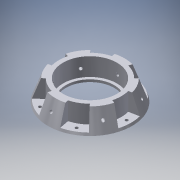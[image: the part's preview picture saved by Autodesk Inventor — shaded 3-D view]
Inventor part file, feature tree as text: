
AUTODESK INVENTOR PART (.ipt)
format: ipt  version: 2017 (Build 210142000, 142)  size: 261,120 bytes
history: native  units: in
note: dims shown in document units (in); Inventor stores cm internally (conversion verified against a paired STEP export)
features: sketch x6, extrude x3, hole x2, pattern_circular x2, plane x1, draft x1, projected_geometry x1
ambient origin geometry x8: Origin, YZ Plane, XZ Plane, XY Plane, X Axis, Y Axis, Z Axis, Center Point
bodies: Solid1 (feature_tree)
feature tree (16):
  extrude  "Extrusion1"  Depth=7.0in
  extrude  "Extrusion4"  Depth=5.21in
  hole  "Hole4"  [1 undecoded]
  pattern_circular  "Circular Pattern4"  Count=6 Angle=360.0deg
  extrude  "Extrusion5"  TaperAngle=30.0deg  [1 undecoded]
  plane  "Work Plane4"
  hole  "Hole5"  [1 undecoded]
  pattern_circular  "Circular Pattern5"  [2 undecoded]
  sketch  "Sketch13"  dims[d55=0.25in d56=0.75in d57=0.375in d58=0.25in d59=0.5635in d60=1.0in d61=0.8108in d62=2.3622in d63=360.0deg d71=30.0deg d72=1.5in d73=0.0in d74=0.85in d75=0.25in d76=0.25in d77=0.75in d78=0.375in d79=0.25in d80=0.5635in d81=2.0in d82=0.0in d83=2.3622in d84=360.0deg d86=0.1374in d12=1.0in d13=1.0in]
  draft  "FaceDraft1"
  sketch  "Sketch1"  dims[d0=4.026in d1=7.0in]
  sketch  "Sketch2"  dims[d2=0.2in d3=0.0in d4=5.21in]
  sketch  "Sketch9"  dims[d47=4.5in d48=1.5in d49=0.0in]
  sketch  "Sketch11"  dims[d52=0.895in]
  sketch  "Sketch12"  dims[d54=0.25in]
  projected_geometry  "Projected Loop1"
note: 5 required parameter values undecoded (feature->parameter linkage not recoverable at this tier; creation-order binding heuristic only, values carry confidence <= 0.55)
